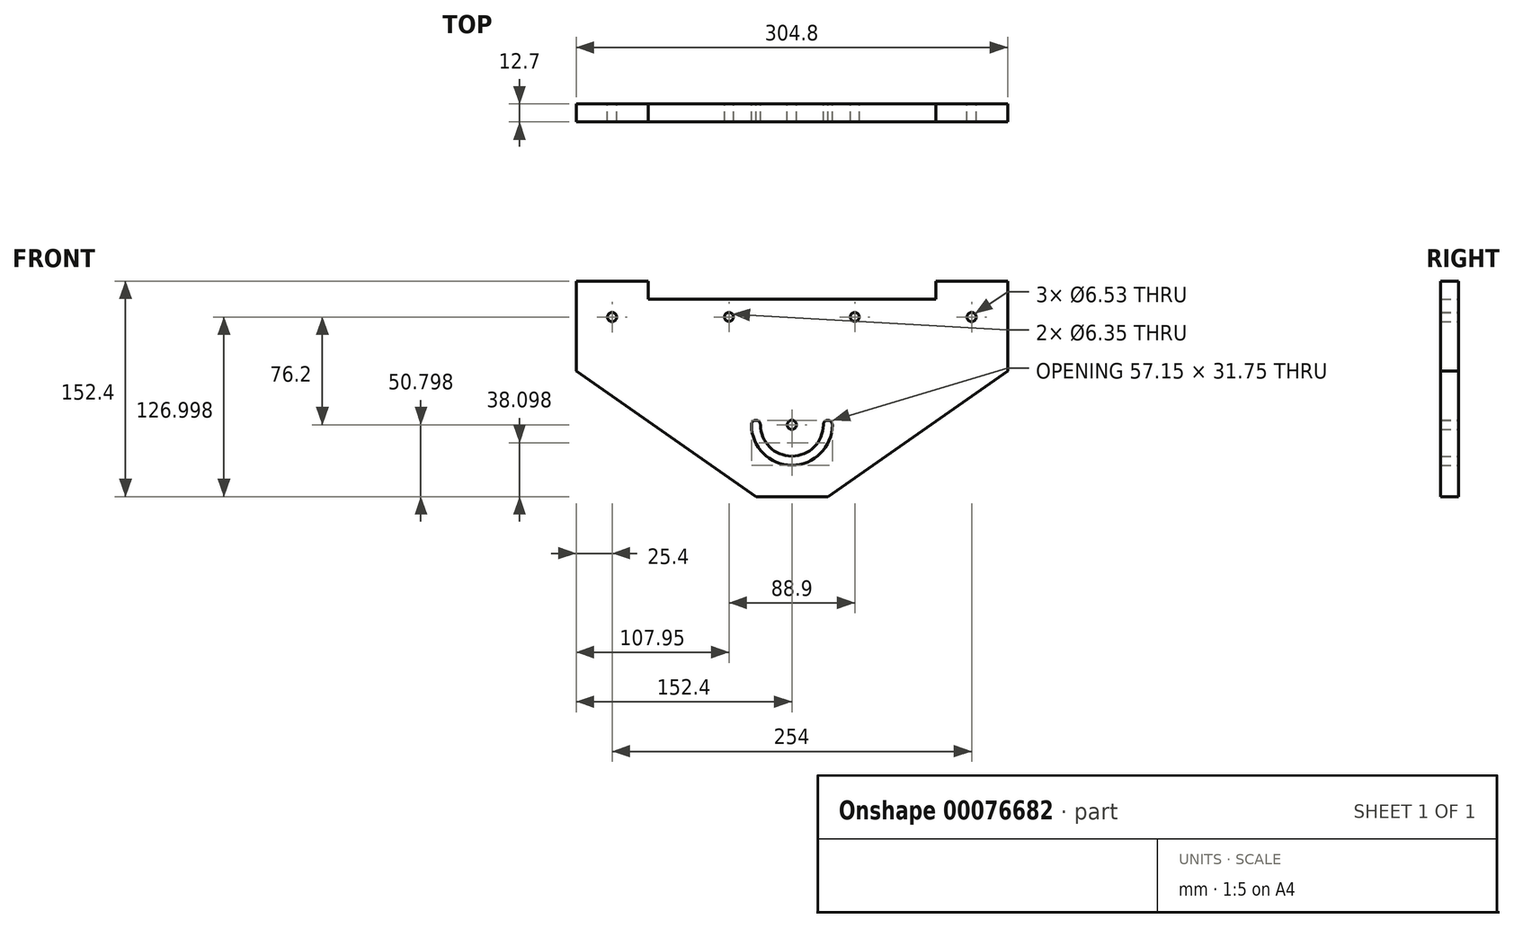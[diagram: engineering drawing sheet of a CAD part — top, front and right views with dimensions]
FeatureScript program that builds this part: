
annotation { "Feature Type Name" : "Feature", "Feature Type Description" : "" }
export const myFeature = defineFeature(function(context is Context, id is Id, definition is map)
    precondition{}
    {
        {
            var Q0;
            Q0=qCreatedBy(makeId("Front.planeOp"),FACE);
            var sketch = newSketch(context, id + "F0", { "sketchPlane" : qUnion([Q0])});
            skLineSegment(sketch, "E0", {"start": v(0, 70.75) * mm, "end": v(0, -101.94) * mm, "construction": true});
            skLineSegment(sketch, "E1", {"start": v(0, 70.75) * mm, "end": v(-101.6, 70.75) * mm});
            skLineSegment(sketch, "E2", {"start": v(-101.6, 70.75) * mm, "end": v(-101.6, 83.45) * mm});
            skLineSegment(sketch, "E3", {"start": v(-101.6, 83.45) * mm, "end": v(-152.4, 83.45) * mm});
            skLineSegment(sketch, "E4", {"start": v(-152.4, 83.45) * mm, "end": v(-152.4, 19.95) * mm});
            skLineSegment(sketch, "E5", {"start": v(0, 70.75) * mm, "end": v(0, -68.95) * mm});
            skLineSegment(sketch, "E6", {"start": v(0, -68.95) * mm, "end": v(-25.4, -68.95) * mm});
            skLineSegment(sketch, "E7", {"start": v(-25.4, -68.95) * mm, "end": v(-152.4, 19.95) * mm});
            skLineSegment(sketch, "E8.MirrorCS", {"start": v(0, 70.75) * mm, "end": v(101.6, 70.75) * mm});
            skLineSegment(sketch, "E9.MirrorCS", {"start": v(101.6, 70.75) * mm, "end": v(101.6, 83.45) * mm});
            skLineSegment(sketch, "E10.MirrorCS", {"start": v(101.6, 83.45) * mm, "end": v(152.4, 83.45) * mm});
            skLineSegment(sketch, "E11.MirrorCS", {"start": v(152.4, 83.45) * mm, "end": v(152.4, 19.95) * mm});
            skLineSegment(sketch, "E12.MirrorCS", {"start": v(25.4, -68.95) * mm, "end": v(152.4, 19.95) * mm});
            skLineSegment(sketch, "E13.MirrorCS", {"start": v(0, -68.95) * mm, "end": v(25.4, -68.95) * mm});
            skLineSegment(sketch, "E14.4", {"start": v(127, 58.05) * mm, "end": v(127, 58.05) * mm});
            skLineSegment(sketch, "E15", {"start": v(0, -68.95) * mm, "end": v(0, -18.15) * mm});
            skLineSegment(sketch, "E16", {"start": v(0, 70.75) * mm, "end": v(0, 51.7) * mm});
            skCircle(sketch, "E17", {"center": v(127, 58.05) * mm, "radius": 25.4 * mm, "construction": true});
            skCircle(sketch, "E18.MirrorC", {"center": v(-127, 58.05) * mm, "radius": 25.4 * mm, "construction": true});
            skArc(sketch, "E19", {"start": v(-22.23, -18.15) * mm, "mid": v(0, -40.38) * mm, "end": v(22.23, -18.15) * mm});
            skArc(sketch, "E20", {"start": v(-28.57, -18.15) * mm, "mid": v(0, -46.73) * mm, "end": v(28.57, -18.15) * mm});
            skPoint(sketch, "E21.orphan", {"position": v(28.57, -18.15) * mm});
            skArc(sketch, "E22", {"start": v(28.57, -18.15) * mm, "mid": v(25.4, -14.98) * mm, "end": v(22.23, -18.15) * mm});
            skArc(sketch, "E23.MirrorCS", {"start": v(-28.57, -18.15) * mm, "mid": v(-25.4, -14.98) * mm, "end": v(-22.23, -18.15) * mm});
            skLineSegment(sketch, "E24.0", {"start": v(0, 58.05) * mm, "end": v(101.6, 58.05) * mm, "construction": true});
            skLineSegment(sketch, "E25.0", {"start": v(0, 58.05) * mm, "end": v(-101.6, 58.05) * mm, "construction": true});
            skLineSegment(sketch, "E26.0", {"start": v(-44.45, 70.75) * mm, "end": v(-44.45, -68.95) * mm, "construction": true});
            skLineSegment(sketch, "E27.0", {"start": v(44.45, 70.75) * mm, "end": v(44.45, -68.95) * mm, "construction": true});
            skCircle(sketch, "E28", {"center": v(44.45, 58.05) * mm, "radius": 3.18 * mm, "construction": true});
            skCircle(sketch, "E29", {"center": v(-44.45, 58.05) * mm, "radius": 3.18 * mm, "construction": true});
            skSolve(sketch);
        }
        {
            var Q0;
            {var subQ7=sQuery(id+"F0.wireOp",EDGE,"E1");Q0=makeQuery(id+"F0.imprint","IMPRINT",FACE,{"disambiguationData":[TD([[makeQuery(id+"F0.imprint","IMPRINT",EDGE,{"derivedFrom":subQ7}),1.0]])]});}
            var Q1;
            {var subQ0=sQuery(id+"F0.wireOp",EDGE,"E8.MirrorCS");Q1=makeQuery(id+"F0.imprint","IMPRINT",FACE,{"disambiguationData":[TD([[makeQuery(id+"F0.imprint","IMPRINT",EDGE,{"derivedFrom":subQ0}),-1.0]])]});}
            extrude(context, id + "F1", {"entities" : qUnion([Q0, Q1]), "depth" : 12.7 * mm});
        }
        {
            var Q0;
            Q0=sQuery(id+"F0.wireOp",VERTEX,"E28.center");
            var Q1;
            Q1=sQuery(id+"F0.wireOp",VERTEX,"E29.center");
            var Q2;
            Q2=makeQuery(id+"F1.opExtrude","SWEPT_BODY",BODY,{"disambiguationData":[OSD([sQuery(id+"F0.wireOp",EDGE,"E1"),sQuery(id+"F0.wireOp",EDGE,"E2"),sQuery(id+"F0.wireOp",EDGE,"E3"),sQuery(id+"F0.wireOp",EDGE,"E4"),sQuery(id+"F0.wireOp",EDGE,"E6"),sQuery(id+"F0.wireOp",EDGE,"E7"),sQuery(id+"F0.wireOp",EDGE,"E8.MirrorCS"),sQuery(id+"F0.wireOp",EDGE,"E9.MirrorCS"),sQuery(id+"F0.wireOp",EDGE,"E10.MirrorCS"),sQuery(id+"F0.wireOp",EDGE,"E11.MirrorCS"),sQuery(id+"F0.wireOp",EDGE,"E12.MirrorCS"),sQuery(id+"F0.wireOp",EDGE,"E13.MirrorCS"),sQuery(id+"F0.wireOp",EDGE,"jr6JAcZG-ykKZ-micM-CKq7-8CDRU7QgzUL2"),sQuery(id+"F0.wireOp",EDGE,"4LmME5ti-7S5q-e4eo-6RZu-4jzve8JVksiU"),sQuery(id+"F0.wireOp",EDGE,"65d66511-7f0c-4e07-8b90-6725448c28da0.MirrorC"),sQuery(id+"F0.wireOp",EDGE,"zFPjhFEn-Ekai-M0AX-jvP7-1sQYl32oihUr"),sQuery(id+"F0.wireOp",EDGE,"E19"),sQuery(id+"F0.wireOp",EDGE,"E20"),sQuery(id+"F0.wireOp",EDGE,"E22"),sQuery(id+"F0.wireOp",EDGE,"E23.MirrorCS")])]});
            hole(context, id + "F2", {"style" : HoleStyle.SIMPLE, "endStyle" : HoleEndStyle.THROUGH, "oppositeDirection" : true, "holeDiameter" : 6.35 * mm, "locations" : qUnion([Q0, Q1]), "scope" : qUnion([Q2]), "isTappedThrough" : true});
        }
        {
            var Q0;
            Q0=sQuery(id+"F0.wireOp",VERTEX,"E18.MirrorC.center");
            var Q1;
            Q1=makeQuery(id+"F1.opExtrude","SWEPT_BODY",BODY,{"disambiguationData":[OSD([sQuery(id+"F0.wireOp",EDGE,"E1"),sQuery(id+"F0.wireOp",EDGE,"E2"),sQuery(id+"F0.wireOp",EDGE,"E3"),sQuery(id+"F0.wireOp",EDGE,"E4"),sQuery(id+"F0.wireOp",EDGE,"E6"),sQuery(id+"F0.wireOp",EDGE,"E7"),sQuery(id+"F0.wireOp",EDGE,"E8.MirrorCS"),sQuery(id+"F0.wireOp",EDGE,"E9.MirrorCS"),sQuery(id+"F0.wireOp",EDGE,"E10.MirrorCS"),sQuery(id+"F0.wireOp",EDGE,"E11.MirrorCS"),sQuery(id+"F0.wireOp",EDGE,"E12.MirrorCS"),sQuery(id+"F0.wireOp",EDGE,"E13.MirrorCS"),sQuery(id+"F0.wireOp",EDGE,"jr6JAcZG-ykKZ-micM-CKq7-8CDRU7QgzUL2"),sQuery(id+"F0.wireOp",EDGE,"4LmME5ti-7S5q-e4eo-6RZu-4jzve8JVksiU"),sQuery(id+"F0.wireOp",EDGE,"zFPjhFEn-Ekai-M0AX-jvP7-1sQYl32oihUr"),sQuery(id+"F0.wireOp",EDGE,"E19"),sQuery(id+"F0.wireOp",EDGE,"E20"),sQuery(id+"F0.wireOp",EDGE,"E22"),sQuery(id+"F0.wireOp",EDGE,"E23.MirrorCS")])]});
            hole(context, id + "F3", {"style" : HoleStyle.SIMPLE, "endStyle" : HoleEndStyle.THROUGH, "oppositeDirection" : true, "standardTappedOrClearance" : lookupTablePath({ "standard" : "ANSI", "fit" : "Close", "size" : "1/4", "type" : "Clearance" }), "standardBlindInLast" : lookupTablePath({ "fit" : "Close", "standard" : "ANSI", "size" : "1/4", "type" : "Clearance" }), "holeDiameter" : 6.53 * mm, "locations" : qUnion([Q0]), "scope" : qUnion([Q1]), "isTappedThrough" : true});
        }
        {
            var Q0;
            Q0=sQuery(id+"F0.wireOp",VERTEX,"E19.center");
            var Q1;
            Q1=makeQuery(id+"F1.opExtrude","SWEPT_BODY",BODY,{"disambiguationData":[OSD([sQuery(id+"F0.wireOp",EDGE,"E1"),sQuery(id+"F0.wireOp",EDGE,"E2"),sQuery(id+"F0.wireOp",EDGE,"E3"),sQuery(id+"F0.wireOp",EDGE,"E4"),sQuery(id+"F0.wireOp",EDGE,"E6"),sQuery(id+"F0.wireOp",EDGE,"E7"),sQuery(id+"F0.wireOp",EDGE,"E8.MirrorCS"),sQuery(id+"F0.wireOp",EDGE,"E9.MirrorCS"),sQuery(id+"F0.wireOp",EDGE,"E10.MirrorCS"),sQuery(id+"F0.wireOp",EDGE,"E11.MirrorCS"),sQuery(id+"F0.wireOp",EDGE,"E12.MirrorCS"),sQuery(id+"F0.wireOp",EDGE,"E13.MirrorCS"),sQuery(id+"F0.wireOp",EDGE,"E19"),sQuery(id+"F0.wireOp",EDGE,"E20"),sQuery(id+"F0.wireOp",EDGE,"E22"),sQuery(id+"F0.wireOp",EDGE,"E23.MirrorCS")])]});
            hole(context, id + "F4", {"style" : HoleStyle.SIMPLE, "endStyle" : HoleEndStyle.THROUGH, "oppositeDirection" : true, "standardTappedOrClearance" : lookupTablePath({ "standard" : "ANSI", "fit" : "Close", "size" : "1/4", "type" : "Clearance" }), "standardBlindInLast" : lookupTablePath({ "fit" : "Close", "standard" : "ANSI", "size" : "1/4", "type" : "Clearance" }), "holeDiameter" : 6.53 * mm, "locations" : qUnion([Q0]), "scope" : qUnion([Q1]), "isTappedThrough" : true});
        }
        {
            var Q0;
            Q0=sQuery(id+"F0.wireOp",VERTEX,"E17.center");
            var Q1;
            Q1=makeQuery(id+"F1.opExtrude","SWEPT_BODY",BODY,{"disambiguationData":[OSD([sQuery(id+"F0.wireOp",EDGE,"E1"),sQuery(id+"F0.wireOp",EDGE,"E2"),sQuery(id+"F0.wireOp",EDGE,"E3"),sQuery(id+"F0.wireOp",EDGE,"E4"),sQuery(id+"F0.wireOp",EDGE,"E6"),sQuery(id+"F0.wireOp",EDGE,"E7"),sQuery(id+"F0.wireOp",EDGE,"E8.MirrorCS"),sQuery(id+"F0.wireOp",EDGE,"E9.MirrorCS"),sQuery(id+"F0.wireOp",EDGE,"E10.MirrorCS"),sQuery(id+"F0.wireOp",EDGE,"E11.MirrorCS"),sQuery(id+"F0.wireOp",EDGE,"E12.MirrorCS"),sQuery(id+"F0.wireOp",EDGE,"E13.MirrorCS"),sQuery(id+"F0.wireOp",EDGE,"E19"),sQuery(id+"F0.wireOp",EDGE,"E20"),sQuery(id+"F0.wireOp",EDGE,"E22"),sQuery(id+"F0.wireOp",EDGE,"E23.MirrorCS")])]});
            hole(context, id + "F5", {"style" : HoleStyle.SIMPLE, "endStyle" : HoleEndStyle.THROUGH, "oppositeDirection" : true, "standardTappedOrClearance" : lookupTablePath({ "standard" : "ANSI", "fit" : "Close", "size" : "1/4", "type" : "Clearance" }), "standardBlindInLast" : lookupTablePath({ "fit" : "Close", "standard" : "ANSI", "size" : "1/4", "type" : "Clearance" }), "holeDiameter" : 6.53 * mm, "locations" : qUnion([Q0]), "scope" : qUnion([Q1]), "isTappedThrough" : true});
        }
    });
